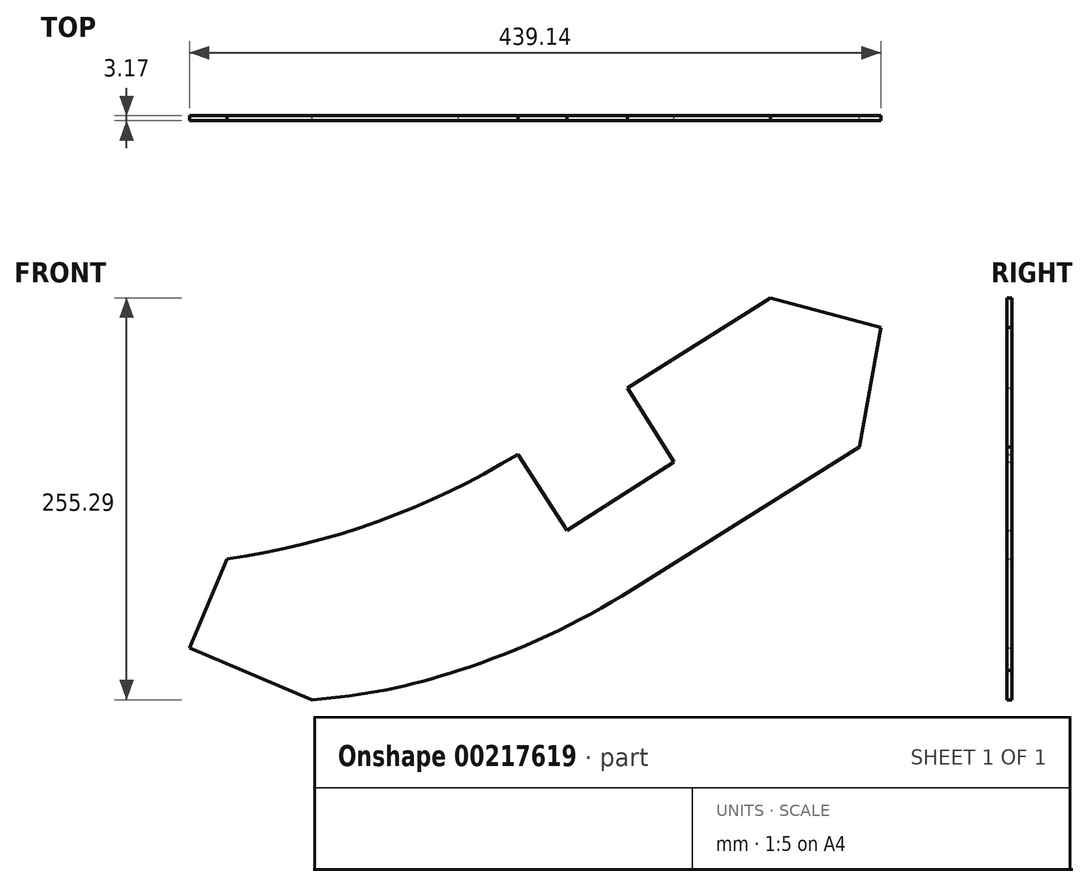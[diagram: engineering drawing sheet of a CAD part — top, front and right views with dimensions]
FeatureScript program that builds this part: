
annotation { "Feature Type Name" : "Feature", "Feature Type Description" : "" }
export const myFeature = defineFeature(function(context is Context, id is Id, definition is map)
    precondition{}
    {
        {
            var Q0;
            Q0=qCreatedBy(makeId("Front.planeOp"),FACE);
            var sketch = newSketch(context, id + "F0", { "sketchPlane" : qUnion([Q0])});
            skLineSegment(sketch, "E0", {"start": v(13.4, 32.95) * mm, "end": v(42.95, -14.12) * mm});
            skLineSegment(sketch, "E1", {"start": v(42.95, -14.12) * mm, "end": v(-25.1, -57.71) * mm});
            skLineSegment(sketch, "E2", {"start": v(-25.1, -57.71) * mm, "end": v(-56.15, -9.23) * mm});
            skArc(sketch, "E3", {"start": v(-240.75, -75.8) * mm, "mid": v(-145.05, -51.95) * mm, "end": v(-56.15, -9.23) * mm});
            skLineSegment(sketch, "E4", {"start": v(13.4, 32.95) * mm, "end": v(104.4, 90.1) * mm});
            skLineSegment(sketch, "E5", {"start": v(160.9, -4.5) * mm, "end": v(174.41, 71.2) * mm});
            skLineSegment(sketch, "E6", {"start": v(174.41, 71.2) * mm, "end": v(104.4, 90.1) * mm});
            skLineSegment(sketch, "E7", {"start": v(160.9, -4.5) * mm, "end": v(16.46, -95.2) * mm});
            skArc(sketch, "E8", {"start": v(-93.89, -146.59) * mm, "mid": v(-37.1, -124.34) * mm, "end": v(16.46, -95.2) * mm});
            skArc(sketch, "E9", {"start": v(-186.8, -165.19) * mm, "mid": v(-139.76, -158.82) * mm, "end": v(-93.89, -146.59) * mm});
            skLineSegment(sketch, "E10", {"start": v(-240.75, -75.8) * mm, "end": v(-264.73, -132.28) * mm});
            skLineSegment(sketch, "E11", {"start": v(-186.8, -165.19) * mm, "end": v(-264.73, -132.28) * mm});
            skSolve(sketch);
        }
        {
            var Q0;
            Q0 = qSketchRegion(id + "F0", true);
            extrude(context, id + "F1", {"entities" : qUnion([Q0]), "depth" : 3.17 * mm});
        }
    });
